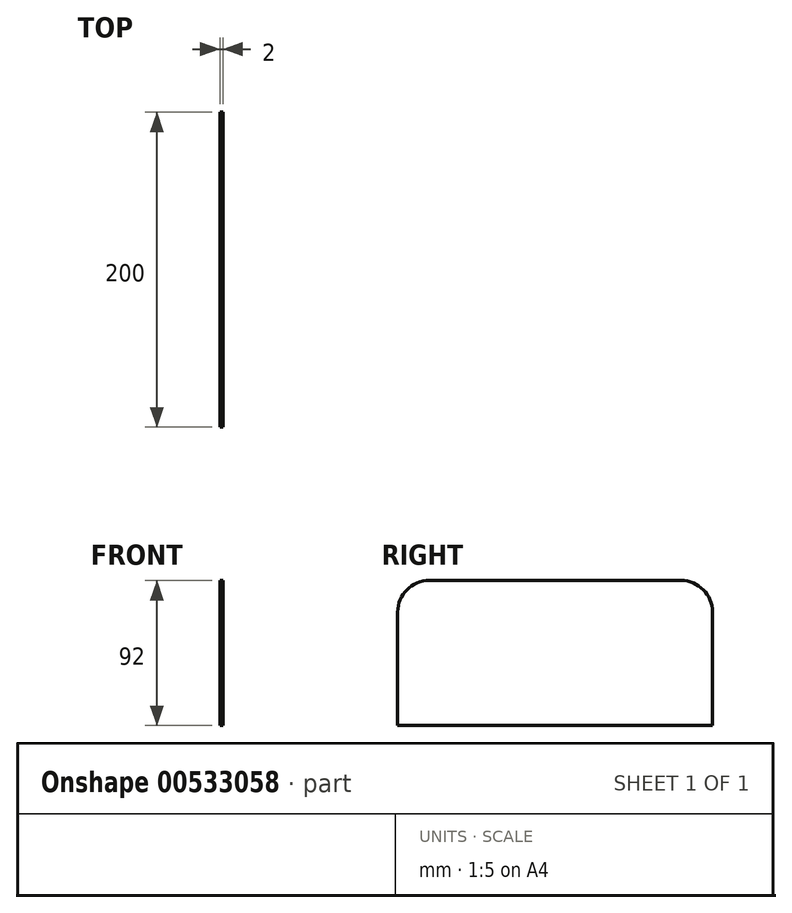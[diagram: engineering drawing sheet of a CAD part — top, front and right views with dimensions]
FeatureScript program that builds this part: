
annotation { "Feature Type Name" : "Feature", "Feature Type Description" : "" }
export const myFeature = defineFeature(function(context is Context, id is Id, definition is map)
    precondition{}
    {
        {
            var Q0;
            Q0=qCreatedBy(makeId("Top.planeOp"),FACE);
            var sketch = newSketch(context, id + "F0", { "sketchPlane" : qUnion([Q0])});
            skLineSegment(sketch, "E0.bottom", {"start": v(1, -100) * mm, "end": v(-1, -100) * mm});
            skLineSegment(sketch, "E0.top", {"start": v(1, 100) * mm, "end": v(-1, 100) * mm});
            skLineSegment(sketch, "E0.left", {"start": v(1, -100) * mm, "end": v(1, 100) * mm});
            skLineSegment(sketch, "E0.right", {"start": v(-1, -100) * mm, "end": v(-1, 100) * mm});
            skPoint(sketch, "E0.middle", {"position": v(0, 0) * mm});
            skSolve(sketch);
        }
        {
            var Q0;
            Q0 = qSketchRegion(id + "F0", true);
            extrude(context, id + "F1", {"entities" : qUnion([Q0]), "depth" : 92 * mm, "offsetDistance" : 25 * mm});
        }
        {
            var Q0;
            Q0=makeQuery(id+"F1.opExtrude","CAP_EDGE",EDGE,{"disambiguationData":[OSD([sQuery(id+"F0.wireOp",EDGE,"E0.bottom")])],"isStart":false});
            var Q1;
            Q1=makeQuery(id+"F1.opExtrude","CAP_EDGE",EDGE,{"disambiguationData":[OSD([sQuery(id+"F0.wireOp",EDGE,"E0.top")])],"isStart":false});
            fillet(context, id + "F2", {"entities" : qUnion([Q0, Q1]), "radius" : 20 * mm, "tangentPropagation" : true, "allowEdgeOverflow" : false});
        }
    });
